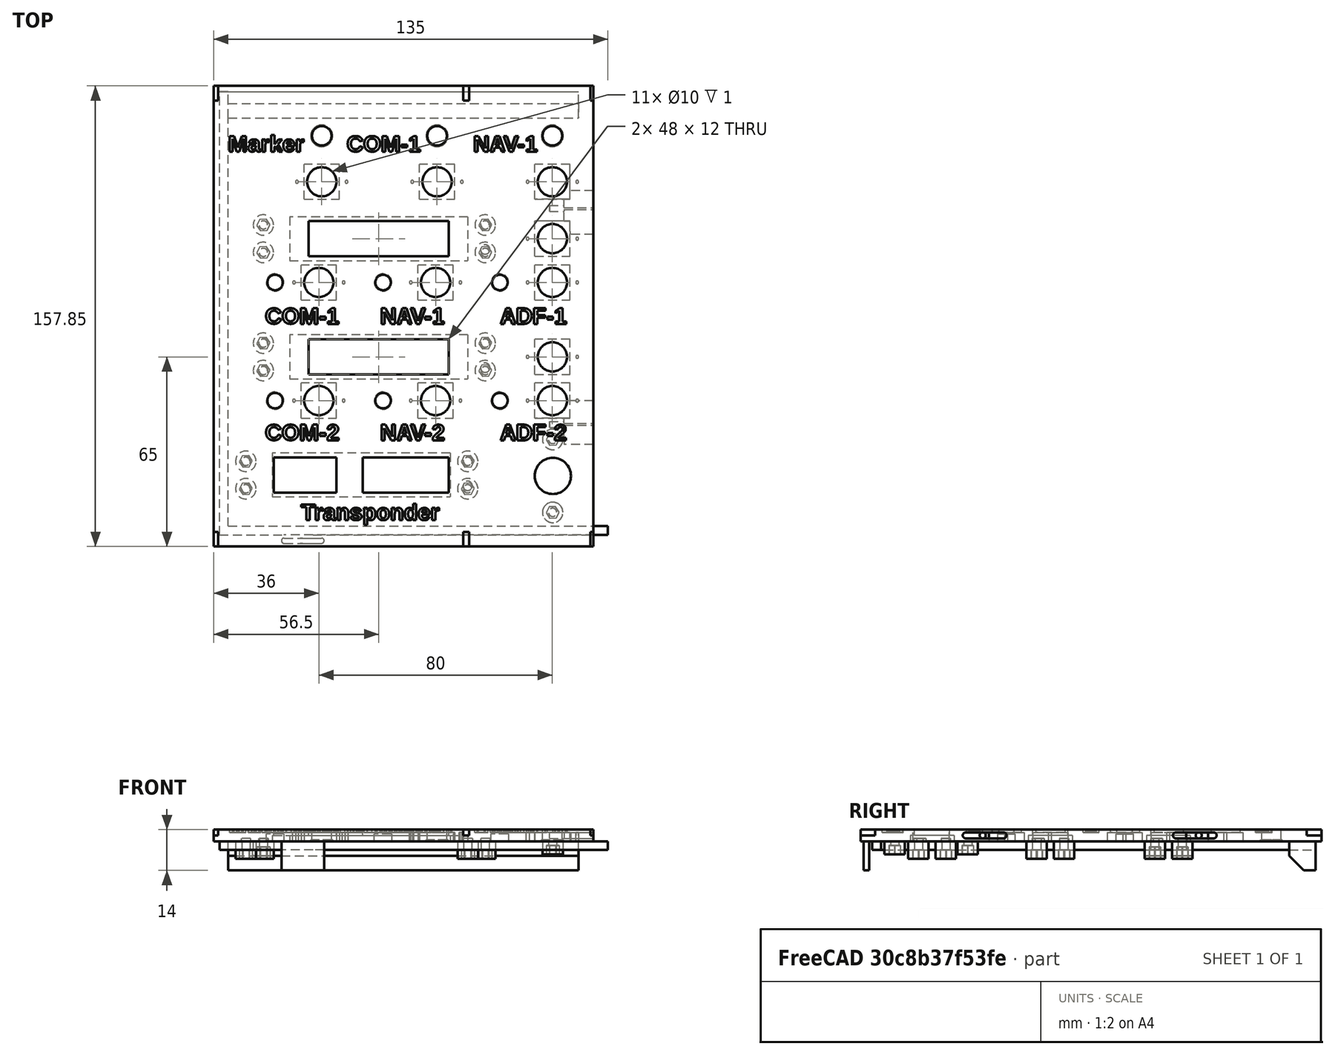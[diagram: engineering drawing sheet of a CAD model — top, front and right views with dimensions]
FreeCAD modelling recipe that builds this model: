
FCSTD DOCUMENT  (FreeCAD 0.17R13522 (Git))
Label: panel_frente_izquierdo
License: CreativeCommons Attribution-ShareAlike
LicenseURL: http://creativecommons.org/licenses/by-sa/4.0/
objects: Part::Cut×18, Part::Feature×17, Part::Box×10, Part::Fuse×6, Part::MultiFuse×2
note: 53 computed .brp shape members not serialized (recipe doc carries the construction recipe); baked Part::Feature solids carry a one-line shape summary decoded from their .brp

FEATURE [Part::Feature] Cut001001001002003001008002002033001001001001001001001002001001002001045001  label="Cut001001001002003001008002002033001001001001001001001002001001002001046"
  shape: bbox 135 x 157.9 x 19 mm, 1304 faces (baked)
FEATURE [Part::Feature] Cut001001001002003001008002002033001001001001001001001002001001002001045002001  label="transponder_part001"
  Placement = pos=(-6,0,0) rot=(0,0,1;0rad)
  shape: bbox 88.15 x 29 x 10 mm, 314 faces (baked)
FEATURE [Part::Box] Box  label="Cube"
  AttacherType = Attacher::AttachEngine3D
  Height = 100
  Length = 88.15
  Placement = pos=(7,3,-195) rot=(0,0,1;0rad)
  Width = 29
FEATURE [Part::Cut] Cut
  Base = -> Cut001001001002003001008002002033001001001001001001001002001001002001045001
  Refine = true
  Tool = -> Box
FEATURE [Part::Fuse] Fusion
  Base = -> Cut001001001002003001008002002033001001001001001001001002001001002001045002001
  Refine = true
  Tool = -> Cut
FEATURE [Part::Box] Box001  label="Cube001"
  AttacherType = Attacher::AttachEngine3D
  Height = 10
  Length = 10
  Placement = pos=(92.2,6.96,-117) rot=(0,0,1;0rad)
  Width = 24
FEATURE [Part::Cut] Cut001001001002003001008002002033001001001001001001001002001001002001045002002
  Base = -> Fusion
  Refine = true
  Tool = -> Box001
FEATURE [Part::Box] Box002  label="Cube002"
  AttacherType = Attacher::AttachEngine3D
  Height = 4
  Length = 4
  Placement = pos=(92,2,-107) rot=(0,0,1;0rad)
  Width = 31
FEATURE [Part::Fuse] Fusion001  label="panel_izquierdo_sin_correr_encoder"
  Base = -> Cut001001001002003001008002002033001001001001001001001002001001002001045002002
  Refine = true
  Tool = -> Box002
FEATURE [Part::Box] Box003  label="Cube003"
  AttacherType = Attacher::AttachEngine3D
  Height = 10
  Length = 14
  Placement = pos=(115,10,-109) rot=(0,0,1;0rad)
  Width = 20
FEATURE [Part::Cut] Cut001001001002003001008002002033001001001001001001001002001001002001045002003
  Base = -> Fusion001
  Refine = true
  Tool = -> Box003
FEATURE [Part::Box] Box004  label="Cube004"
  AttacherType = Attacher::AttachEngine3D
  Height = 10
  Length = 10
  Placement = pos=(117,4,-117) rot=(0,0,1;0rad)
  Width = 10
FEATURE [Part::Feature] Box004001  label="Cube005"
  Placement = pos=(117,28,-117) rot=(0,0,1;0rad)
  shape: bbox 10 x 10 x 10 mm, 6 faces (baked)
FEATURE [Part::Cut] Cut001001001002003001008002002033001001001001001001001002001001002001045002004
  Base = -> Cut001001001002003001008002002033001001001001001001001002001001002001045002003
  Refine = true
  Tool = -> Box004
FEATURE [Part::Cut] Cut001001001002003001008002002033001001001001001001001002001001002001045002005
  Base = -> Cut001001001002003001008002002033001001001001001001001002001001002001045002004
  Refine = true
  Tool = -> Box004001
FEATURE [Part::Box] Box004002  label="Cube006"
  AttacherType = Attacher::AttachEngine3D
  Height = 1
  Length = 5
  Placement = pos=(119,5,-107) rot=(0,0,1;0rad)
  Width = 5
FEATURE [Part::Feature] Box004002001  label="Cube007"
  Placement = pos=(119,31,-107) rot=(0,0,1;0rad)
  shape: bbox 5 x 5 x 1 mm, 6 faces (baked)
FEATURE [Part::Fuse] Fusion002
  Base = -> Cut001001001002003001008002002033001001001001001001001002001001002001045002005
  Refine = true
  Tool = -> Box004002001
FEATURE [Part::Fuse] Fusion003
  Base = -> Box004002
  Refine = true
  Tool = -> Fusion002
FEATURE [Part::Feature] Cut001001001002003001008002002033001001001001001001001002001001002001045002003002  label="doble_cncoder_tra12_soportes001"
  Placement = pos=(-6,0,0) rot=(0,0,1;0rad)
  shape: bbox 22 x 44 x 8.5 mm, 39 faces (baked)
FEATURE [Part::Box] Box004002002  label="Cube008"
  AttacherType = Attacher::AttachEngine3D
  Height = 10
  Length = 18
  Placement = pos=(107,10,-109) rot=(0,0,1;0rad)
  Width = 20
FEATURE [Part::Cut] Cut001001001002003001008002002033001001001001001001001002001001002001045002003003
  Base = -> Fusion003
  Refine = true
  Tool = -> Box004002002
FEATURE [Part::Fuse] Fusion004
  Base = -> Cut001001001002003001008002002033001001001001001001001002001001002001045002003002
  Refine = true
  Tool = -> Cut001001001002003001008002002033001001001001001001001002001001002001045002003003
FEATURE [Part::Box] Box004002003  label="Cube009"
  AttacherType = Attacher::AttachEngine3D
  Height = 4
  Length = 6
  Placement = pos=(123,8,-107) rot=(0,0,1;0rad)
  Width = 24
FEATURE [Part::Fuse] Fusion005  label="panel_izquierdo_sin_apya_flejes"
  Base = -> Fusion004
  Refine = true
  Tool = -> Box004002003
FEATURE [Part::Box] Box004002004  label="apoya_fleje_lateral_1"
  AttacherType = Attacher::AttachEngine3D
  Height = 2
  Length = 1.5
  Placement = pos=(0,-4,-105) rot=(0,0,1;0rad)
  Width = 5
FEATURE [Part::Feature] Box004002004001  label="apoya_fleje_lateral_002"
  Placement = pos=(0,148.85,-105) rot=(0,0,1;0rad)
  shape: bbox 1.5 x 5 x 2 mm, 6 faces (baked)
FEATURE [Part::Feature] Box004002004001001  label="apoya_fleje_lateral_003"
  Placement = pos=(85.5,148.85,-105) rot=(0,0,1;0rad)
  shape: bbox 1.5 x 5 x 2 mm, 6 faces (baked)
FEATURE [Part::Feature] Box004002004001001001  label="apoya_fleje_lateral_004"
  Placement = pos=(86,148.85,-105) rot=(0,0,1;0rad)
  shape: bbox 1.5 x 5 x 2 mm, 6 faces (baked)
FEATURE [Part::Feature] Box004002004001001001001  label="apoya_fleje_lateral_005"
  Placement = pos=(129,148.85,-105) rot=(0,0,1;0rad)
  shape: bbox 1.5 x 5 x 2 mm, 6 faces (baked)
FEATURE [Part::Feature] Box004002004001001001002  label="apoya_fleje_lateral_006"
  Placement = pos=(85.5,-4,-105) rot=(0,0,1;0rad)
  shape: bbox 1.5 x 5 x 2 mm, 6 faces (baked)
FEATURE [Part::Feature] Box004002004001001001002001  label="apoya_fleje_lateral_007"
  Placement = pos=(86,-4,-105) rot=(0,0,1;0rad)
  shape: bbox 1.5 x 5 x 2 mm, 6 faces (baked)
FEATURE [Part::Feature] Box004002004001001001002001001  label="apoya_fleje_lateral_008"
  Placement = pos=(129,-4,-105) rot=(0,0,1;0rad)
  shape: bbox 1.5 x 5 x 2 mm, 6 faces (baked)
FEATURE [Part::Cut] Cut001001001002003001008002002033001001001001001001001002001001002001045002003004
  Base = -> Fusion005
  Refine = true
  Tool = -> Box004002004
FEATURE [Part::Cut] Cut001001001002003001008002002033001001001001001001001002001001002001045002003005
  Base = -> Cut001001001002003001008002002033001001001001001001001002001001002001045002003004
  Refine = true
  Tool = -> Box004002004001
FEATURE [Part::Cut] Cut001001001002003001008002002033001001001001001001001002001001002001045002003006
  Base = -> Cut001001001002003001008002002033001001001001001001001002001001002001045002003005
  Refine = true
  Tool = -> Box004002004001001
FEATURE [Part::Cut] Cut001001001002003001008002002033001001001001001001001002001001002001045002003007
  Base = -> Cut001001001002003001008002002033001001001001001001001002001001002001045002003006
  Refine = true
  Tool = -> Box004002004001001001
FEATURE [Part::Cut] Cut001001001002003001008002002033001001001001001001001002001001002001045002003008
  Base = -> Cut001001001002003001008002002033001001001001001001001002001001002001045002003007
  Refine = true
  Tool = -> Box004002004001001001001
FEATURE [Part::Cut] Cut001001001002003001008002002033001001001001001001001002001001002001045002003009
  Base = -> Cut001001001002003001008002002033001001001001001001001002001001002001045002003008
  Refine = true
  Tool = -> Box004002004001001001002
FEATURE [Part::Cut] Cut001001001002003001008002002033001001001001001001001002001001002001045002003010
  Base = -> Cut001001001002003001008002002033001001001001001001001002001001002001045002003009
  Refine = true
  Tool = -> Box004002004001001001002001
FEATURE [Part::Cut] Cut001001001002003001008002002033001001001001001001001002001001002001045002003011
  Base = -> Cut001001001002003001008002002033001001001001001001001002001001002001045002003010
  Refine = true
  Tool = -> Box004002004001001001002001001
FEATURE [Part::Feature] Body001  label="cortador_parea_encastres"
  Placement = pos=(120,32,-105) rot=(0.57735,0.57735,0.57735;2.0944rad)
  shape: bbox 20 x 15 x 2 mm, 6 faces (baked)
FEATURE [Part::Feature] Body001001  label="cortador_parea_encastres001"
  Placement = pos=(120,104,-105) rot=(0.57735,0.57735,0.57735;2.0944rad)
  shape: bbox 20 x 15 x 2 mm, 6 faces (baked)
FEATURE [Part::Cut] Cut001001001002003001008002002033001001001001001001001002001001002001045002003012
  Base = -> Cut001001001002003001008002002033001001001001001001001002001001002001045002003011
  Tool = -> Body001
FEATURE [Part::Cut] Cut001001001002003001008002002033001001001001001001001002001001002001045002003013
  Base = -> Cut001001001002003001008002002033001001001001001001001002001001002001045002003012
  Tool = -> Body001001
FEATURE [Part::Feature] Body002  label="encastres001"
  Placement = pos=(24.1,-2,-123) rot=(0,0,1;0rad)
  shape: bbox 14.6 x 1.8 x 20 mm, 6 faces (baked)
FEATURE [Part::Box] Box004002004001001001002001002  label="Cube010"
  AttacherType = Attacher::AttachEngine3D
  Height = 19
  Length = 10
  Placement = pos=(24,-7,-126) rot=(0,0,1;0rad)
  Width = 7
FEATURE [Part::Feature] Box004002004001001001002001002001  label="Cube011"
  Placement = pos=(32,-7,-136) rot=(0,0,1;0rad)
  shape: bbox 10 x 7 x 19 mm, 6 faces (baked)
FEATURE [Part::Cut] Cut001001001002003001008002002033001001001001001001001002001001002001045002003014
  Base = -> Cut001001001002003001008002002033001001001001001001001002001001002001045002003013
  Tool = -> Box004002004001001001002001002
FEATURE [Part::Feature] Box004002004001001001002001002001001  label="Cube012"
  Placement = pos=(22,-7,-136) rot=(0,0,1;0rad)
  shape: bbox 10 x 7 x 19 mm, 6 faces (baked)
FEATURE [Part::MultiFuse] Fusion006
  Shapes = -> [Box004002004001001001002001002001,Box004002004001001001002001002001001]
FEATURE [Part::Cut] Cut001001001002003001008002002033001001001001001001001002001001002001045002003015
  Base = -> Body002
  Tool = -> Fusion006
FEATURE [Part::MultiFuse] Fusion007  label="panel izq"
  Shapes = -> [Cut001001001002003001008002002033001001001001001001001002001001002001045002003014,Cut001001001002003001008002002033001001001001001001001002001001002001045002003015]
